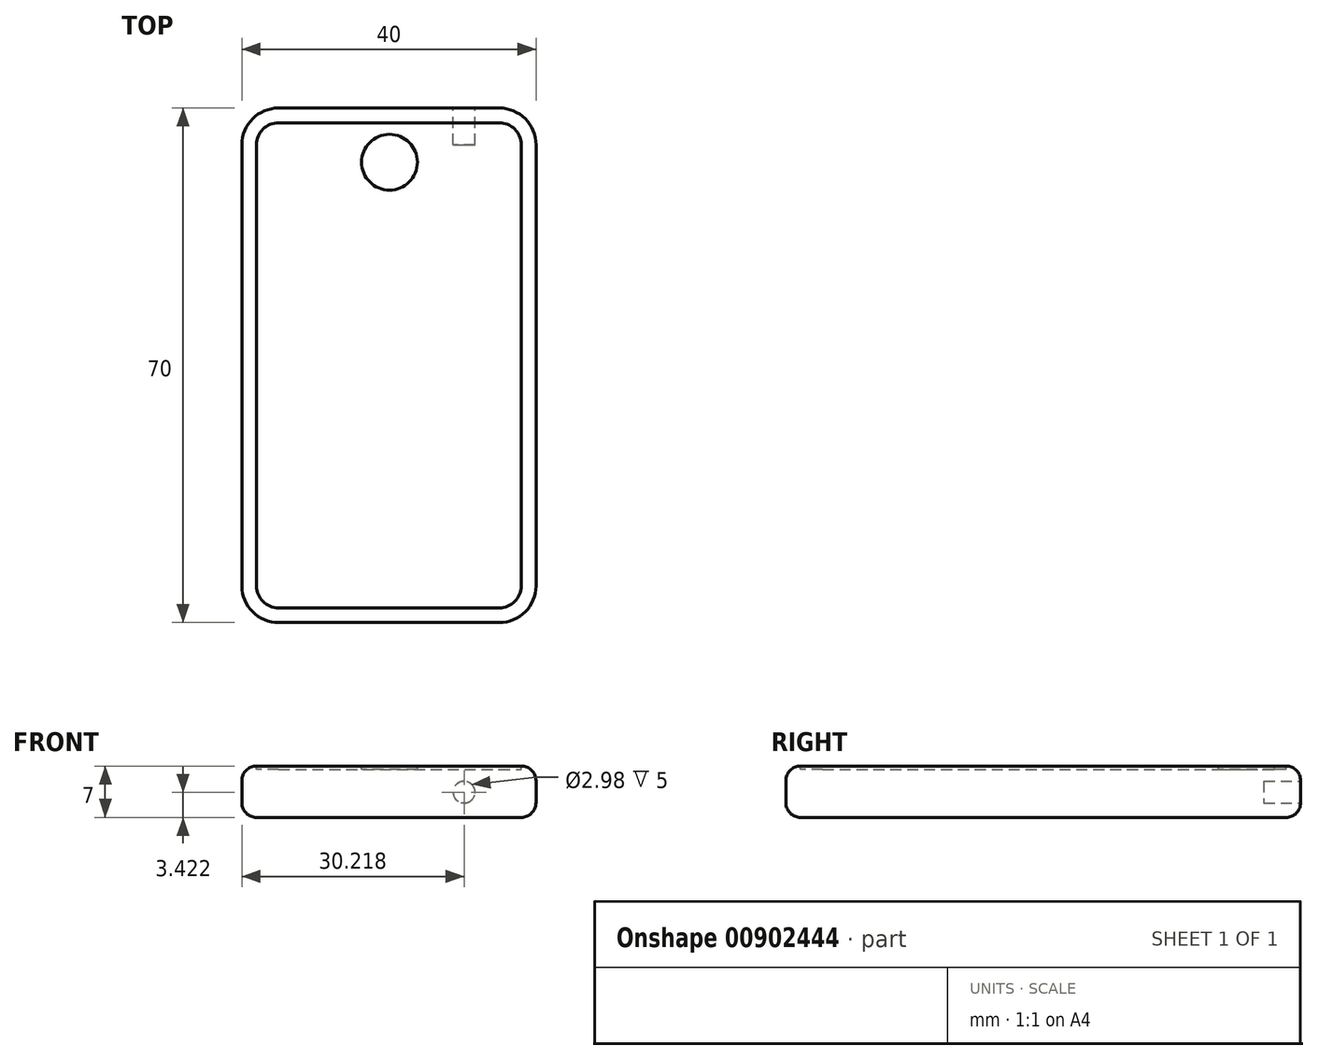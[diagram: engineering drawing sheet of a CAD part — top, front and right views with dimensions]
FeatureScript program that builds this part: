
annotation { "Feature Type Name" : "Feature", "Feature Type Description" : "" }
export const myFeature = defineFeature(function(context is Context, id is Id, definition is map)
    precondition{}
    {
        {
            var Q0;
            Q0=qCreatedBy(makeId("Top.planeOp"),FACE);
            var sketch = newSketch(context, id + "F0", { "sketchPlane" : qUnion([Q0])});
            skLineSegment(sketch, "E0.bottom", {"start": v(0, 0) * mm, "end": v(40, 0) * mm});
            skLineSegment(sketch, "E0.top", {"start": v(0, 70) * mm, "end": v(40, 70) * mm});
            skLineSegment(sketch, "E0.left", {"start": v(0, 0) * mm, "end": v(0, 70) * mm});
            skLineSegment(sketch, "E0.right", {"start": v(40, 0) * mm, "end": v(40, 70) * mm});
            skSolve(sketch);
        }
        {
            var Q0;
            Q0=makeQuery(id+"F0.imprint","IMPRINT",FACE,{"disambiguationData":[TD([[makeQuery(id+"F0.imprint","IMPRINT",EDGE,{"derivedFrom":sQuery(id+"F0.wireOp",EDGE,"E0.bottom")}),1.0]])]});
            extrude(context, id + "F1", {"entities" : qUnion([Q0]), "depth" : 7 * mm, "offsetDistance" : 25 * mm});
        }
        {
            var Q0;
            Q0=makeQuery(id+"F1.opExtrude","SWEPT_EDGE",EDGE,{"disambiguationData":[OSD([sQuery(id+"F0.wireOp",EDGE,"E0.top"),sQuery(id+"F0.wireOp",EDGE,"E0.right")])]});
            var Q1;
            Q1=makeQuery(id+"F1.opExtrude","SWEPT_EDGE",EDGE,{"disambiguationData":[OSD([sQuery(id+"F0.wireOp",EDGE,"E0.top"),sQuery(id+"F0.wireOp",EDGE,"E0.left")])]});
            var Q2;
            Q2=makeQuery(id+"F1.opExtrude","SWEPT_EDGE",EDGE,{"disambiguationData":[OSD([sQuery(id+"F0.wireOp",EDGE,"E0.bottom"),sQuery(id+"F0.wireOp",EDGE,"E0.left")])]});
            var Q3;
            Q3=makeQuery(id+"F1.opExtrude","SWEPT_EDGE",EDGE,{"disambiguationData":[OSD([sQuery(id+"F0.wireOp",EDGE,"E0.bottom"),sQuery(id+"F0.wireOp",EDGE,"E0.right")])]});
            fillet(context, id + "F2", {"entities" : qUnion([Q0, Q1, Q2, Q3]), "radius" : 5 * mm, "tangentPropagation" : true, "allowEdgeOverflow" : false});
        }
        {
            var Q0;
            Q0=makeQuery(id+"F1.opExtrude","SWEPT_FACE",FACE,{"disambiguationData":[OSD([sQuery(id+"F0.wireOp",EDGE,"E0.top")])]});
            var sketch = newSketch(context, id + "F3", { "sketchPlane" : qUnion([Q0])});
            skCircle(sketch, "E1", {"center": v(-30.22, 3.42) * mm, "radius": 1.49 * mm});
            skSolve(sketch);
        }
        {
            var Q0;
            Q0=makeQuery(id+"F3.imprint","IMPRINT",FACE,{"disambiguationData":[TD([[makeQuery(id+"F3.imprint","IMPRINT",EDGE,{"derivedFrom":sQuery(id+"F3.wireOp",EDGE,"E1")}),1.0]])]});
            extrude(context, id + "F4", {"entities" : qUnion([Q0]), "operationType" : NewBodyOperationType.REMOVE, "oppositeDirection" : true, "depth" : 5 * mm, "offsetDistance" : 25 * mm});
        }
        {
            var Q0;
            Q0=makeQuery(id+"F1.opExtrude","CAP_EDGE",EDGE,{"disambiguationData":[OSD([sQuery(id+"F0.wireOp",EDGE,"E0.right")])],"isStart":true});
            var Q1;
            Q1=makeQuery(id+"F1.opExtrude","CAP_EDGE",EDGE,{"disambiguationData":[OSD([sQuery(id+"F0.wireOp",EDGE,"E0.left")])],"isStart":false});
            fillet(context, id + "F5", {"entities" : qUnion([Q0, Q1]), "radius" : 2 * mm, "tangentPropagation" : true, "allowEdgeOverflow" : false});
        }
        {
            var Q0;
            Q0=makeQuery(id+"F1.opExtrude","CAP_FACE",FACE,{"disambiguationData":[OSD([sQuery(id+"F0.wireOp",EDGE,"E0.bottom"),sQuery(id+"F0.wireOp",EDGE,"E0.top"),sQuery(id+"F0.wireOp",EDGE,"E0.left"),sQuery(id+"F0.wireOp",EDGE,"E0.right")])],"isStart":false});
            var sketch = newSketch(context, id + "F6", { "sketchPlane" : qUnion([Q0])});
            skPoint(sketch, "E2.centerSnap0", {"position": v(20, 68) * mm});
            skCircle(sketch, "E3", {"center": v(20.08, 62.63) * mm, "radius": 3.8 * mm});
            skSolve(sketch);
        }
        {
            var Q0;
            Q0=makeQuery(id+"F6.imprint","IMPRINT",FACE,{"disambiguationData":[TD([[makeQuery(id+"F6.imprint","IMPRINT",EDGE,{"derivedFrom":sQuery(id+"F6.wireOp",EDGE,"E3")}),-1.0]])]});
            extrude(context, id + "F7", {"entities" : qUnion([Q0]), "operationType" : NewBodyOperationType.REMOVE, "oppositeDirection" : true, "depth" : 0.5 * mm, "offsetDistance" : 25 * mm});
        }
    });
